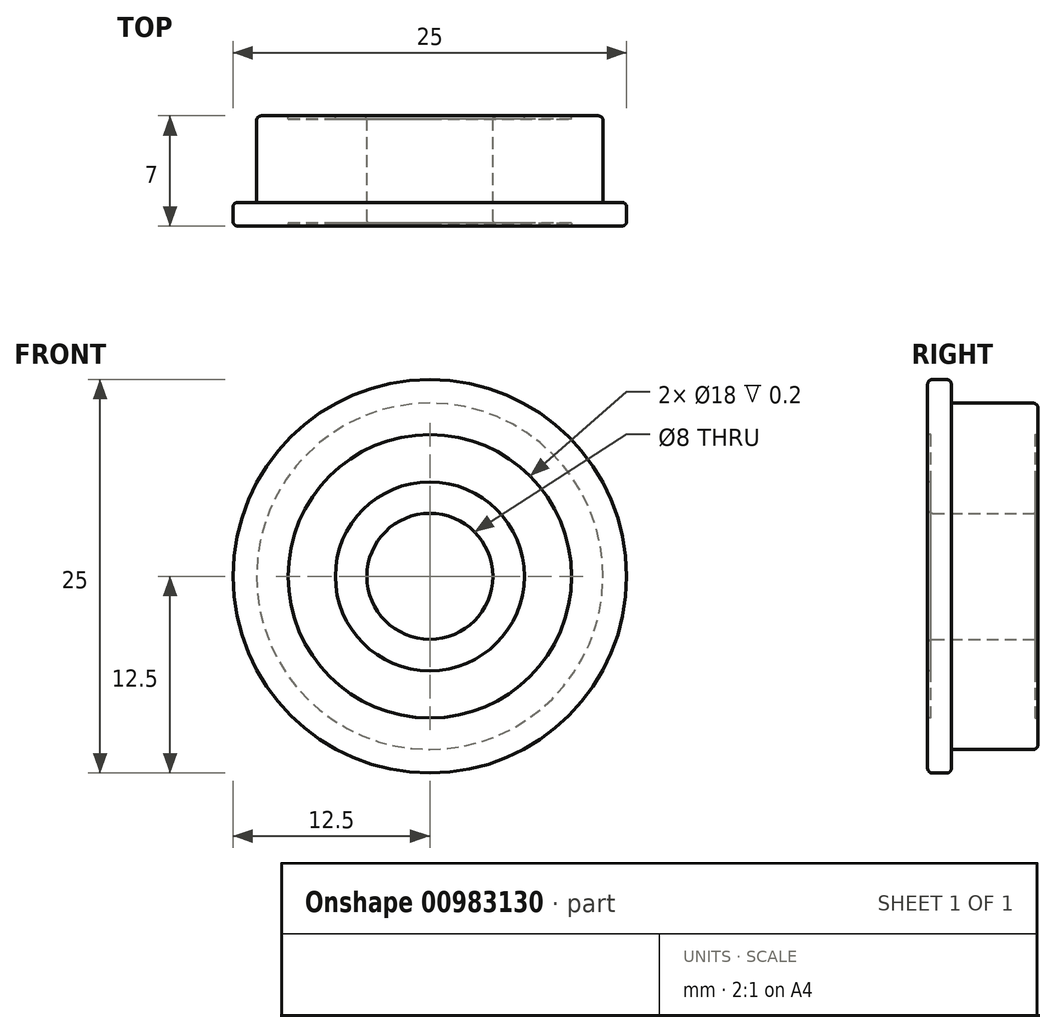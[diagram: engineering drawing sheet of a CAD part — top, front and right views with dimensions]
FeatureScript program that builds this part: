
annotation { "Feature Type Name" : "Feature", "Feature Type Description" : "" }
export const myFeature = defineFeature(function(context is Context, id is Id, definition is map)
    precondition{}
    {
        {
            var Q0;
            Q0=qCreatedBy(makeId("Front.planeOp"),FACE);
            var sketch = newSketch(context, id + "F0", { "sketchPlane" : qUnion([Q0])});
            skCircle(sketch, "E0", {"center": v(0, 0) * mm, "radius": 11 * mm});
            skCircle(sketch, "E1", {"center": v(0, 0) * mm, "radius": 4 * mm});
            skSolve(sketch);
        }
        {
            var Q0;
            Q0=qSketchRegion(id+"F0",true);
            extrude(context, id + "F1", {"entities" : qUnion([Q0]), "depth" : 5.5 * mm, "offsetDistance" : 25 * mm});
        }
        {
            var Q0;
            Q0=makeQuery(id+"F1.opExtrude","CAP_FACE",FACE,{"disambiguationData":[OSD([sQuery(id+"F0.wireOp",EDGE,"E0"),sQuery(id+"F0.wireOp",EDGE,"E1")])],"isStart":false});
            var sketch = newSketch(context, id + "F2", { "sketchPlane" : qUnion([Q0])});
            skCircle(sketch, "E2", {"center": v(0, 0) * mm, "radius": 4 * mm});
            skCircle(sketch, "E3", {"center": v(0, 0) * mm, "radius": 12.5 * mm});
            skSolve(sketch);
        }
        {
            var Q0;
            Q0=qSketchRegion(id+"F2",true);
            extrude(context, id + "F3", {"entities" : qUnion([Q0]), "operationType" : NewBodyOperationType.ADD, "depth" : 1.5 * mm, "offsetDistance" : 25 * mm});
        }
        {
            var Q0;
            Q0=makeQuery(id+"F1.opExtrude","CAP_FACE",FACE,{"disambiguationData":[OSD([sQuery(id+"F0.wireOp",EDGE,"E0"),sQuery(id+"F0.wireOp",EDGE,"E1")])],"isStart":true});
            var sketch = newSketch(context, id + "F4", { "sketchPlane" : qUnion([Q0])});
            skCircle(sketch, "E4", {"center": v(0, 0) * mm, "radius": 6 * mm});
            skCircle(sketch, "E5", {"center": v(0, 0) * mm, "radius": 9 * mm});
            skSolve(sketch);
        }
        {
            var Q0;
            Q0=qSketchRegion(id+"F4",true);
            extrude(context, id + "F5", {"entities" : qUnion([Q0]), "operationType" : NewBodyOperationType.REMOVE, "oppositeDirection" : true, "depth" : 0.2 * mm, "offsetDistance" : 25 * mm});
        }
        {
            var Q0;
            Q0=makeQuery(id+"F3.opExtrude","CAP_FACE",FACE,{"disambiguationData":[OSD([sQuery(id+"F2.wireOp",EDGE,"E2"),sQuery(id+"F2.wireOp",EDGE,"E3")])],"isStart":false});
            var sketch = newSketch(context, id + "F6", { "sketchPlane" : qUnion([Q0])});
            skCircle(sketch, "E6", {"center": v(0, 0) * mm, "radius": 6 * mm});
            skCircle(sketch, "E7", {"center": v(0, 0) * mm, "radius": 9 * mm});
            skSolve(sketch);
        }
        {
            var Q0;
            Q0=qSketchRegion(id+"F6",true);
            extrude(context, id + "F7", {"entities" : qUnion([Q0]), "operationType" : NewBodyOperationType.REMOVE, "oppositeDirection" : true, "depth" : 0.2 * mm, "offsetDistance" : 25 * mm});
        }
        {
            var Q0;
            Q0=makeQuery(id+"F3.opExtrude","CAP_EDGE",EDGE,{"disambiguationData":[OSD([sQuery(id+"F2.wireOp",EDGE,"E3")])],"isStart":false});
            var Q1;
            Q1=makeQuery(id+"F3.opExtrude","CAP_EDGE",EDGE,{"disambiguationData":[OSD([sQuery(id+"F2.wireOp",EDGE,"E3")])],"isStart":true});
            var Q2;
            Q2=makeQuery(id+"F1.opExtrude","CAP_EDGE",EDGE,{"disambiguationData":[OSD([sQuery(id+"F0.wireOp",EDGE,"E0")])],"isStart":true});
            var Q3;
            Q3=makeQuery(id+"F3.opExtrude","CAP_EDGE",EDGE,{"disambiguationData":[OSD([sQuery(id+"F2.wireOp",EDGE,"E2")])],"isStart":false});
            var Q4;
            Q4=makeQuery(id+"F1.opExtrude","CAP_EDGE",EDGE,{"disambiguationData":[OSD([sQuery(id+"F0.wireOp",EDGE,"E1")])],"isStart":true});
            fillet(context, id + "F8", {"entities" : qUnion([Q0, Q1, Q2, Q3, Q4]), "radius" : 0.3 * mm, "tangentPropagation" : true, "allowEdgeOverflow" : false});
        }
    });
